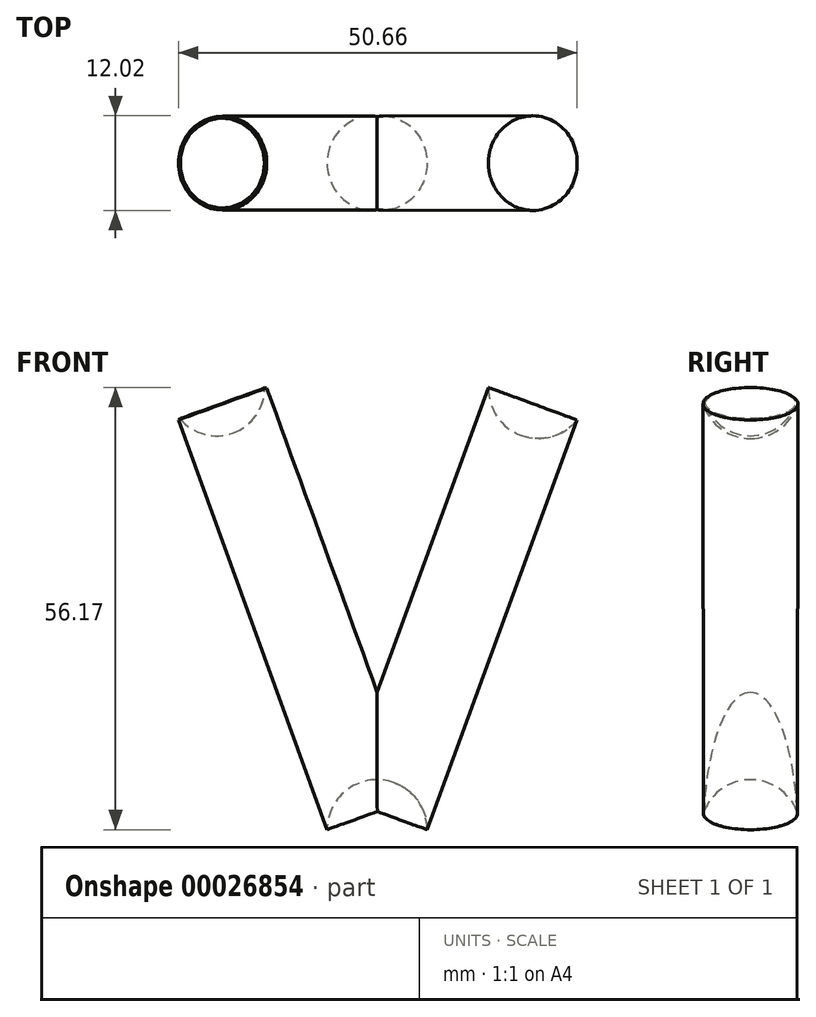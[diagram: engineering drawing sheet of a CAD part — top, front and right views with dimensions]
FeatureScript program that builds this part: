
annotation { "Feature Type Name" : "Feature", "Feature Type Description" : "" }
export const myFeature = defineFeature(function(context is Context, id is Id, definition is map)
    precondition{}
    {
        {
            var Q0;
            Q0=qCreatedBy(makeId("Front.planeOp"),FACE);
            var sketch = newSketch(context, id + "F0", { "sketchPlane" : qUnion([Q0])});
            skArc(sketch, "E0", {"start": v(6.35, 0) * mm, "mid": v(5.2, 3.64) * mm, "end": v(2.18, 5.96) * mm});
            skLineSegment(sketch, "E1.bottom", {"start": v(-6.35, 0) * mm, "end": v(-6.45, 0) * mm});
            skLineSegment(sketch, "E2", {"start": v(-6.45, 0) * mm, "end": v(-6.34, 0.3) * mm});
            skLineSegment(sketch, "E3", {"start": v(6.35, 0) * mm, "end": v(26.85, 55.93) * mm});
            skArc(sketch, "E4", {"start": v(18.3, 50.09) * mm, "mid": v(24.08, 50.81) * mm, "end": v(26.85, 55.93) * mm});
            skLineSegment(sketch, "E5", {"start": v(0, 0) * mm, "end": v(18.3, 50.09) * mm});
            skArc(sketch, "E6.trimOffspring", {"start": v(-6.34, 0.3) * mm, "mid": v(-6.35, 0.15) * mm, "end": v(-6.35, 0) * mm});
            skPoint(sketch, "E7.orphan", {"position": v(14.13, 56.18) * mm});
            skSolve(sketch);
        }
        {
            var Q0;
            {var subQ1=sQuery(id+"F0.wireOp",EDGE,"E3");var subQ5=sQuery(id+"F0.wireOp",EDGE,"E0");var subQ6=makeQuery(id+"F0.imprint","INTERSECT",VERTEX,{"derivedFrom":[subQ5,subQ1]});Q0=makeQuery(id+"F0.imprint","IMPRINT",FACE,{"disambiguationData":[TD([[makeQuery(id+"F0.imprint","IMPRINT",EDGE,{"disambiguationData":[TD([[subQ6,-1.0]])],"derivedFrom":subQ5}),-1.0]])]});}
            var Q1;
            Q1=sQuery(id+"F0.wireOp",EDGE,"E5");
            revolve(context, id + "F1", {"entities" : qUnion([Q0]), "axis" : qUnion([Q1]), "revolveType" : RevolveType.FULL});
        }
        {
            var Q0;
            Q0=qCreatedBy(makeId("Front.planeOp"),FACE);
            var sketch = newSketch(context, id + "F2", { "sketchPlane" : qUnion([Q0])});
            skArc(sketch, "E8", {"start": v(6.35, 0) * mm, "mid": v(3.64, 5.2) * mm, "end": v(-2.17, 5.97) * mm});
            skLineSegment(sketch, "E9", {"start": v(6.35, 0) * mm, "end": v(-14.02, 56.12) * mm});
            skLineSegment(sketch, "E10", {"start": v(-14.29, 56.12) * mm, "end": v(-14.02, 56.12) * mm});
            skLineSegment(sketch, "E11", {"start": v(-18.3, 50.4) * mm, "end": v(-2.17, 5.97) * mm});
            skArc(sketch, "E12.trimOffspring", {"start": v(-18.3, 50.4) * mm, "mid": v(-15.4, 52.63) * mm, "end": v(-14.29, 56.12) * mm});
            skPoint(sketch, "E13.end.orphan", {"position": v(-26.72, 56.12) * mm});
            skPoint(sketch, "E14.orphan", {"position": v(-6.35, 0) * mm});
            skSolve(sketch);
        }
        {
            var Q0;
            {var subQ1=sQuery(id+"F2.wireOp",EDGE,"E10");Q0=makeQuery(id+"F2.imprint","IMPRINT",FACE,{"disambiguationData":[TD([[makeQuery(id+"F2.imprint","IMPRINT",EDGE,{"derivedFrom":subQ1}),-1.0]])]});}
            var Q1;
            Q1=sQuery(id+"F2.wireOp",EDGE,"E11");
            revolve(context, id + "F3", {"operationType" : NewBodyOperationType.ADD, "entities" : qUnion([Q0]), "axis" : qUnion([Q1]), "revolveType" : RevolveType.FULL});
        }
    });
